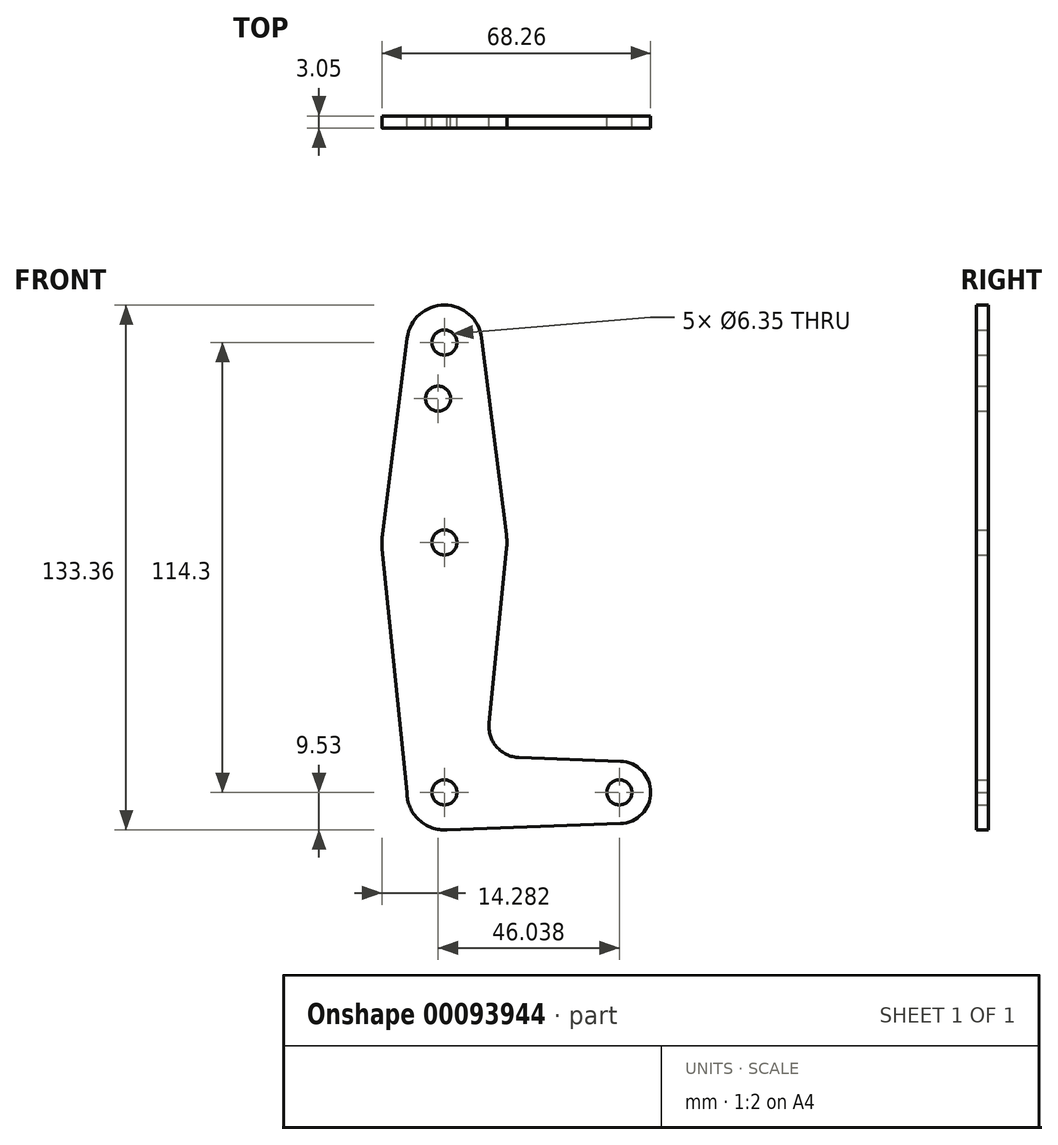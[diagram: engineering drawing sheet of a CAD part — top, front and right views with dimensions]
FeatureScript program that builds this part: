
annotation { "Feature Type Name" : "Feature", "Feature Type Description" : "" }
export const myFeature = defineFeature(function(context is Context, id is Id, definition is map)
    precondition{}
    {
        {
            var Q0;
            Q0=qCreatedBy(makeId("Front.planeOp"),FACE);
            var sketch = newSketch(context, id + "F0", { "sketchPlane" : qUnion([Q0])});
            skCircle(sketch, "E0", {"center": v(0, 0) * mm, "radius": 9.53 * mm});
            skCircle(sketch, "E1", {"center": v(0, 63.5) * mm, "radius": 15.88 * mm});
            skCircle(sketch, "E2", {"center": v(0, 114.3) * mm, "radius": 9.53 * mm});
            skCircle(sketch, "E3", {"center": v(44.45, 0) * mm, "radius": 7.94 * mm});
            skLineSegment(sketch, "E4", {"start": v(44.45, 0) * mm, "end": v(0, 0) * mm, "construction": true});
            skLineSegment(sketch, "E5", {"start": v(-9.45, 115.5) * mm, "end": v(-15.75, 65.48) * mm});
            skLineSegment(sketch, "E6", {"start": v(0, -9.53) * mm, "end": v(44.73, -7.93) * mm});
            skLineSegment(sketch, "E7", {"start": v(9.45, 115.5) * mm, "end": v(15.75, 65.48) * mm});
            skLineSegment(sketch, "E8", {"start": v(15.8, 61.91) * mm, "end": v(11.34, 17.6) * mm});
            skLineSegment(sketch, "E9", {"start": v(18.97, 8.85) * mm, "end": v(44.73, 7.93) * mm});
            skLineSegment(sketch, "E10", {"start": v(0, 114.3) * mm, "end": v(0, 0) * mm, "construction": true});
            skCircle(sketch, "E11", {"center": v(0, 114.3) * mm, "radius": 3.18 * mm});
            skCircle(sketch, "E12", {"center": v(-1.59, 100.03) * mm, "radius": 3.18 * mm});
            skCircle(sketch, "E13", {"center": v(0, 0) * mm, "radius": 3.18 * mm});
            skCircle(sketch, "E14", {"center": v(44.45, 0) * mm, "radius": 3.18 * mm});
            skCircle(sketch, "E15", {"center": v(0, 63.5) * mm, "radius": 3.18 * mm});
            skArc(sketch, "E16.filletArc", {"start": v(11.34, 17.6) * mm, "mid": v(13.26, 11.57) * mm, "end": v(18.97, 8.85) * mm});
            skLineSegment(sketch, "E17", {"start": v(-15.8, 61.9) * mm, "end": v(-9.52, 0) * mm});
            skSolve(sketch);
        }
        {
            var Q0;
            Q0 = qSketchRegion(id + "F0", true);
            extrude(context, id + "F1", {"entities" : qUnion([Q0]), "depth" : 3.05 * mm});
        }
    });
